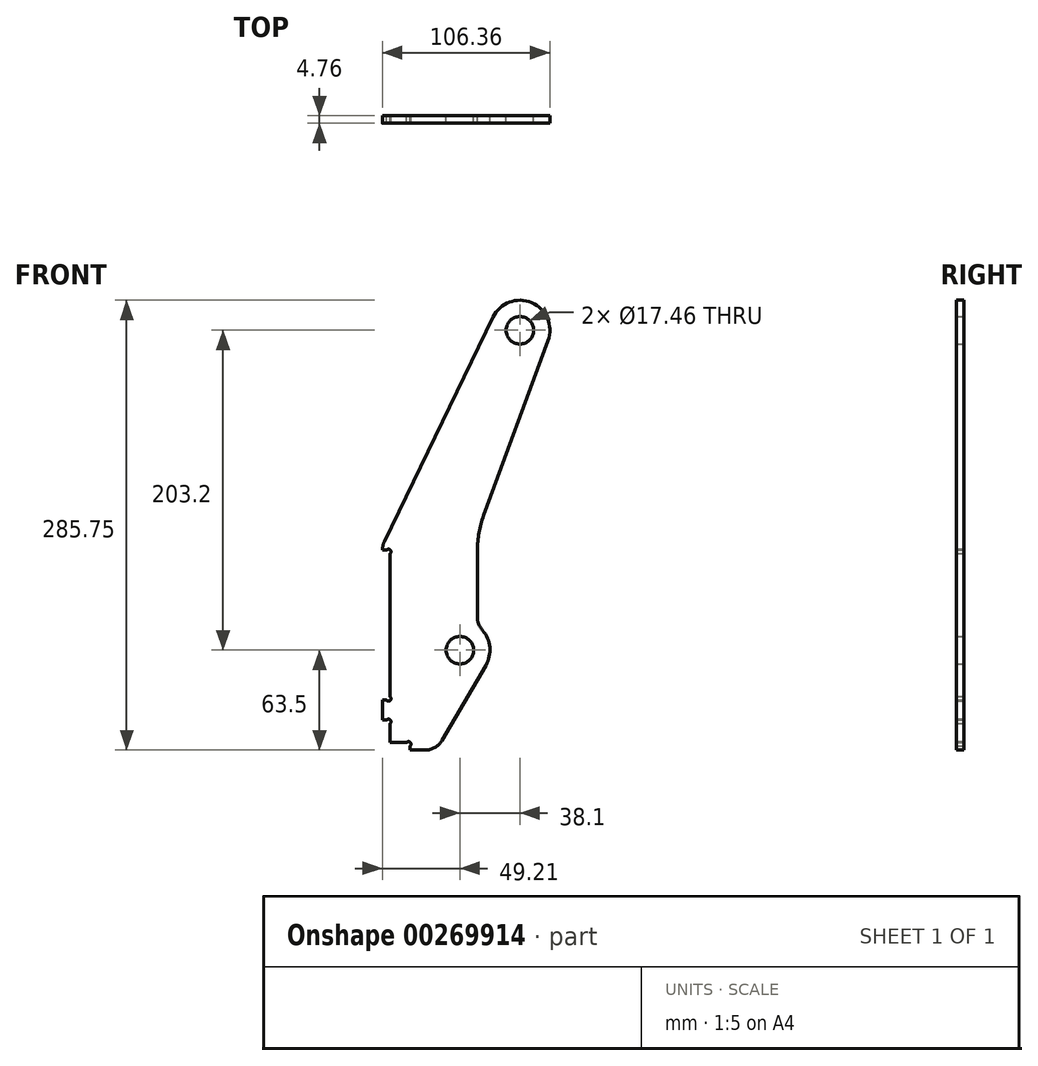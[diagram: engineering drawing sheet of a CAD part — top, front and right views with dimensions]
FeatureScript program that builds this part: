
annotation { "Feature Type Name" : "Feature", "Feature Type Description" : "" }
export const myFeature = defineFeature(function(context is Context, id is Id, definition is map)
    precondition{}
    {
        {
            var Q0;
            Q0=qCreatedBy(makeId("Front.planeOp"),FACE);
            var sketch = newSketch(context, id + "F0", { "sketchPlane" : qUnion([Q0])});
            skCircle(sketch, "E0", {"center": v(0, 0) * mm, "radius": 8.73 * mm});
            skCircle(sketch, "E1", {"center": v(38.1, 203.2) * mm, "radius": 8.73 * mm});
            skLineSegment(sketch, "E2", {"start": v(-44.45, 63.5) * mm, "end": v(-44.45, -58.74) * mm});
            skLineSegment(sketch, "E3", {"start": v(-44.45, 63.5) * mm, "end": v(-49.21, 63.5) * mm});
            skLineSegment(sketch, "E4", {"start": v(-44.45, -58.74) * mm, "end": v(-31.75, -58.74) * mm});
            skLineSegment(sketch, "E5", {"start": v(-31.75, -58.74) * mm, "end": v(-31.75, -63.5) * mm});
            skLineSegment(sketch, "E6", {"start": v(-31.75, -63.5) * mm, "end": v(-22.23, -63.5) * mm});
            skArc(sketch, "E7", {"start": v(16.46, -9.58) * mm, "mid": v(18.96, 1.86) * mm, "end": v(14.29, 12.6) * mm});
            skArc(sketch, "E8", {"start": v(55.98, 196.62) * mm, "mid": v(45.55, 220.73) * mm, "end": v(20.95, 211.5) * mm});
            skArc(sketch, "E9", {"start": v(-47.95, 69.03) * mm, "mid": v(-48.9, 66.34) * mm, "end": v(-49.21, 63.5) * mm});
            skArc(sketch, "E10", {"start": v(-22.23, -63.5) * mm, "mid": v(-15.9, -61.8) * mm, "end": v(-11.25, -57.19) * mm});
            skLineSegment(sketch, "E11", {"start": v(-49.21, 63.5) * mm, "end": v(-49.21, -98) * mm, "construction": true});
            skLineSegment(sketch, "E12", {"start": v(20.95, 211.5) * mm, "end": v(-47.95, 69.03) * mm});
            skLineSegment(sketch, "E13", {"start": v(11.11, 63.5) * mm, "end": v(11.11, 21) * mm});
            skLineSegment(sketch, "E14", {"start": v(55.98, 196.62) * mm, "end": v(15.03, 85.45) * mm});
            skArc(sketch, "E15", {"start": v(11.11, 21) * mm, "mid": v(11.93, 16.51) * mm, "end": v(14.29, 12.6) * mm});
            skLineSegment(sketch, "E16", {"start": v(-11.25, -57.19) * mm, "end": v(16.46, -9.58) * mm});
            skArc(sketch, "E17", {"start": v(15.03, 85.45) * mm, "mid": v(12.1, 74.65) * mm, "end": v(11.11, 63.5) * mm});
            skSolve(sketch);
        }
        {
            var Q0;
            Q0 = qSketchRegion(id + "F0", true);
            extrude(context, id + "F1", {"entities" : qUnion([Q0]), "depth" : 4.76 * mm});
        }
        {
            var Q0;
            Q0=qCreatedBy(makeId("Front.planeOp"),FACE);
            var sketch = newSketch(context, id + "F2", { "sketchPlane" : qUnion([Q0])});
            skLineSegment(sketch, "E18.bottom", {"start": v(-44.45, -44.45) * mm, "end": v(-49.21, -44.45) * mm});
            skLineSegment(sketch, "E18.top", {"start": v(-44.45, -31.75) * mm, "end": v(-49.21, -31.75) * mm});
            skLineSegment(sketch, "E18.left", {"start": v(-44.45, -44.45) * mm, "end": v(-44.45, -31.75) * mm});
            skLineSegment(sketch, "E18.right", {"start": v(-49.21, -44.45) * mm, "end": v(-49.21, -31.75) * mm});
            skSolve(sketch);
        }
        {
            var Q0;
            Q0 = qSketchRegion(id + "F2", true);
            var Q1;
            Q1=makeQuery(id+"F1.opExtrude","CAP_FACE",FACE,{"disambiguationData":[OSD([sQuery(id+"F0.wireOp",EDGE,"E0"),sQuery(id+"F0.wireOp",EDGE,"E1"),sQuery(id+"F0.wireOp",EDGE,"E2"),sQuery(id+"F0.wireOp",EDGE,"E3"),sQuery(id+"F0.wireOp",EDGE,"E4"),sQuery(id+"F0.wireOp",EDGE,"E5"),sQuery(id+"F0.wireOp",EDGE,"E6"),sQuery(id+"F0.wireOp",EDGE,"E7"),sQuery(id+"F0.wireOp",EDGE,"E8"),sQuery(id+"F0.wireOp",EDGE,"E9"),sQuery(id+"F0.wireOp",EDGE,"E10"),sQuery(id+"F0.wireOp",EDGE,"E12"),sQuery(id+"F0.wireOp",EDGE,"E13"),sQuery(id+"F0.wireOp",EDGE,"E14"),sQuery(id+"F0.wireOp",EDGE,"E15"),sQuery(id+"F0.wireOp",EDGE,"E16"),sQuery(id+"F0.wireOp",EDGE,"E17")])],"isStart":false});
            extrude(context, id + "F3", {"entities" : qUnion([Q0]), "operationType" : NewBodyOperationType.ADD, "endBound" : BoundingType.UP_TO_SURFACE, "endBoundEntityFace" : qUnion([Q1]), "depth" : 25.4 * mm});
        }
        {
            var Q0;
            Q0=qCreatedBy(makeId("Front.planeOp"),FACE);
            var sketch = newSketch(context, id + "F4", { "sketchPlane" : qUnion([Q0])});
            skLineSegment(sketch, "E19", {"start": v(-44.45, -44.45) * mm, "end": v(-45.4, -45.4) * mm, "construction": true});
            skLineSegment(sketch, "E20", {"start": v(-31.75, -58.74) * mm, "end": v(-32.7, -59.68) * mm, "construction": true});
            skLineSegment(sketch, "E21", {"start": v(-44.45, 63.5) * mm, "end": v(-45.4, 62.56) * mm, "construction": true});
            skLineSegment(sketch, "E22", {"start": v(-44.45, -31.75) * mm, "end": v(-45.4, -30.8) * mm, "construction": true});
            skCircle(sketch, "E23", {"center": v(-32.7, -59.68) * mm, "radius": 1.59 * mm});
            skCircle(sketch, "E24", {"center": v(-45.4, -45.4) * mm, "radius": 1.59 * mm});
            skCircle(sketch, "E25", {"center": v(-45.4, -30.8) * mm, "radius": 1.59 * mm});
            skCircle(sketch, "E26", {"center": v(-45.4, 62.56) * mm, "radius": 1.59 * mm});
            skSolve(sketch);
        }
        {
            var Q0;
            Q0=makeQuery(id+"F4.imprint","IMPRINT",FACE,{"disambiguationData":[TD([[makeQuery(id+"F4.imprint","IMPRINT",EDGE,{"derivedFrom":sQuery(id+"F4.wireOp",EDGE,"E26")}),1.0]])]});
            var Q1;
            Q1=makeQuery(id+"F4.imprint","IMPRINT",FACE,{"disambiguationData":[TD([[makeQuery(id+"F4.imprint","IMPRINT",EDGE,{"derivedFrom":sQuery(id+"F4.wireOp",EDGE,"E23")}),1.0]])]});
            var Q2;
            Q2=makeQuery(id+"F4.imprint","IMPRINT",FACE,{"disambiguationData":[TD([[makeQuery(id+"F4.imprint","IMPRINT",EDGE,{"derivedFrom":sQuery(id+"F4.wireOp",EDGE,"E24")}),1.0]])]});
            var Q3;
            Q3=makeQuery(id+"F4.imprint","IMPRINT",FACE,{"disambiguationData":[TD([[makeQuery(id+"F4.imprint","IMPRINT",EDGE,{"derivedFrom":sQuery(id+"F4.wireOp",EDGE,"E25")}),1.0]])]});
            extrude(context, id + "F5", {"entities" : qUnion([Q0, Q1, Q2, Q3]), "operationType" : NewBodyOperationType.REMOVE, "endBound" : BoundingType.THROUGH_ALL, "depth" : 25.4 * mm});
        }
    });
